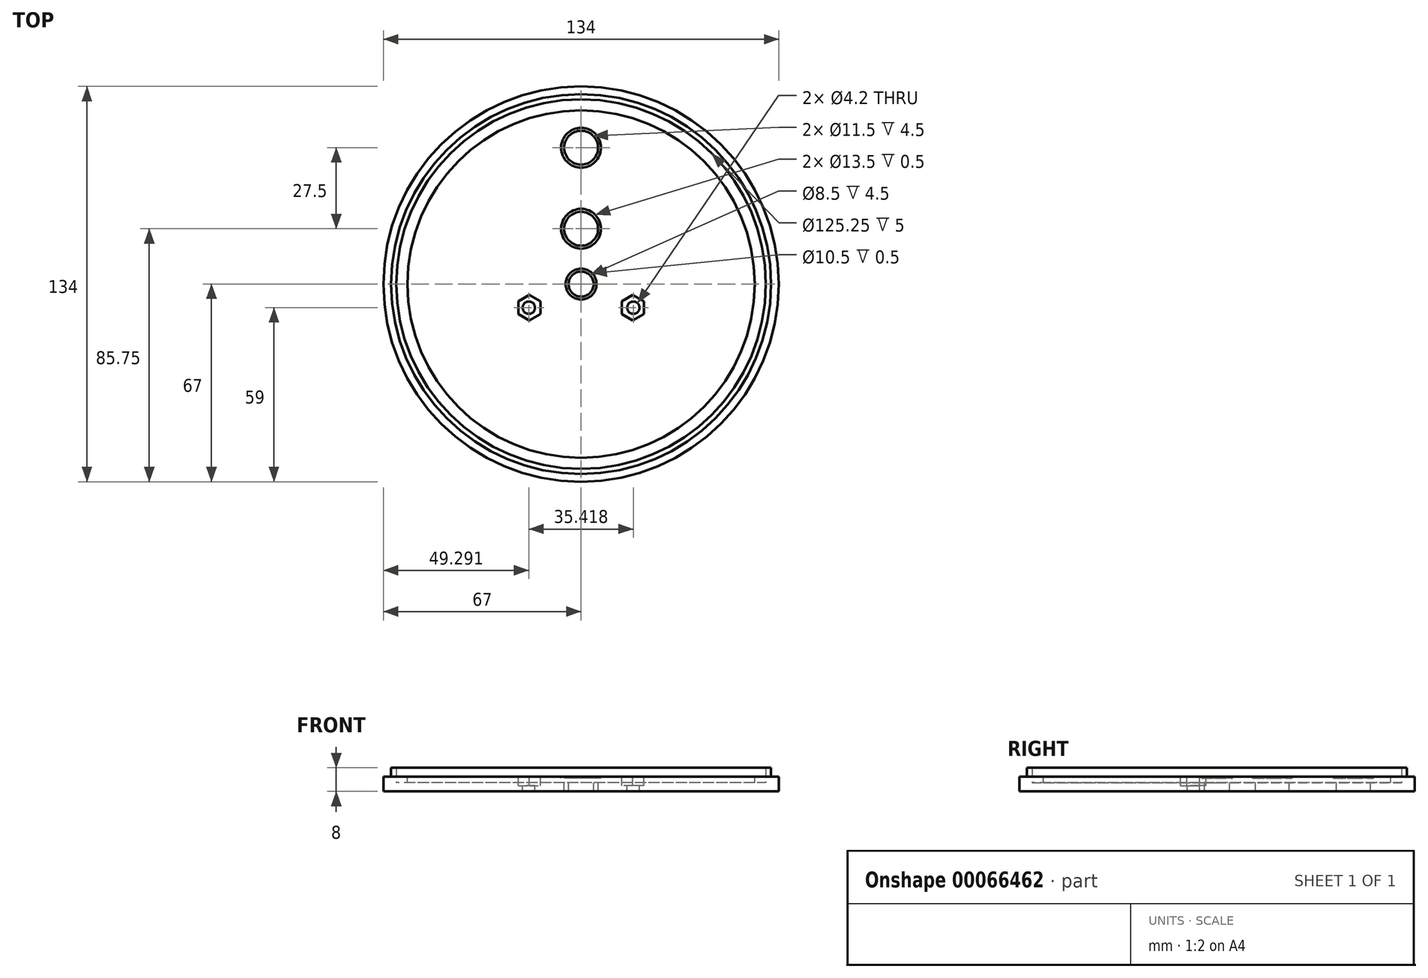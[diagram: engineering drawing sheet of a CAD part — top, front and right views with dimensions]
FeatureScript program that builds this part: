
annotation { "Feature Type Name" : "Feature", "Feature Type Description" : "" }
export const myFeature = defineFeature(function(context is Context, id is Id, definition is map)
    precondition{}
    {
        {
            var Q0;
            Q0=qCreatedBy(makeId("Top.planeOp"),FACE);
            var sketch = newSketch(context, id + "F0", { "sketchPlane" : qUnion([Q0])});
            skCircle(sketch, "E0", {"center": v(0, 0) * mm, "radius": 67 * mm});
            skSolve(sketch);
        }
        {
            var Q0;
            Q0=makeQuery(id+"F0.imprint","IMPRINT",FACE,{"disambiguationData":[TD([[makeQuery(id+"F0.imprint","IMPRINT",EDGE,{"derivedFrom":sQuery(id+"F0.wireOp",EDGE,"E0")}),1.0]])]});
            extrude(context, id + "F1", {"entities" : qUnion([Q0]), "endBound" : BoundingType.SYMMETRIC, "depth" : 5 * mm});
        }
        {
            var Q0;
            Q0=makeQuery(id+"F1.opExtrude","CAP_FACE",FACE,{"disambiguationData":[OSD([sQuery(id+"F0.wireOp",EDGE,"E0")])],"isStart":false});
            var sketch = newSketch(context, id + "F2", { "sketchPlane" : qUnion([Q0])});
            skCircle(sketch, "E1", {"center": v(0, 0) * mm, "radius": 64.38 * mm});
            skSolve(sketch);
        }
        {
            var Q0;
            Q0=makeQuery(id+"F2.imprint","IMPRINT",FACE,{"disambiguationData":[TD([[makeQuery(id+"F2.imprint","IMPRINT",EDGE,{"derivedFrom":sQuery(id+"F2.wireOp",EDGE,"E1")}),1.0]])]});
            var sketch = newSketch(context, id + "F3", { "sketchPlane" : qUnion([Q0])});
            skCircle(sketch, "E2", {"center": v(0, 0) * mm, "radius": 62.62 * mm});
            skSolve(sketch);
        }
        {
            var Q0;
            Q0=makeQuery(id+"F3.imprint","IMPRINT",FACE,{"disambiguationData":[TD([[makeQuery(id+"F3.imprint","IMPRINT",EDGE,{"derivedFrom":sQuery(id+"F3.wireOp",EDGE,"E2")}),-1.0]])]});
            extrude(context, id + "F4", {"entities" : qUnion([Q0]), "operationType" : NewBodyOperationType.ADD, "depth" : 3 * mm});
        }
        {
            var Q0;
            Q0=makeQuery(id+"F3.imprint","IMPRINT",FACE,{"disambiguationData":[TD([[makeQuery(id+"F3.imprint","IMPRINT",EDGE,{"derivedFrom":sQuery(id+"F3.wireOp",EDGE,"E2")}),1.0]])]});
            var sketch = newSketch(context, id + "F5", { "sketchPlane" : qUnion([Q0])});
            skCircle(sketch, "E3", {"center": v(0, 0) * mm, "radius": 58.88 * mm});
            skSolve(sketch);
        }
        {
            var Q0;
            Q0=makeQuery(id+"F5.imprint","IMPRINT",FACE,{"disambiguationData":[TD([[makeQuery(id+"F5.imprint","IMPRINT",EDGE,{"derivedFrom":sQuery(id+"F5.wireOp",EDGE,"E3")}),-1.0]])]});
            extrude(context, id + "F6", {"entities" : qUnion([Q0]), "operationType" : NewBodyOperationType.REMOVE, "oppositeDirection" : true, "depth" : 2 * mm});
        }
        {
            var Q0;
            Q0=makeQuery(id+"F2.imprint","IMPRINT",FACE,{"disambiguationData":[TD([[makeQuery(id+"F2.imprint","IMPRINT",EDGE,{"derivedFrom":sQuery(id+"F2.wireOp",EDGE,"E1")}),-1.0]])]});
            var sketch = newSketch(context, id + "F7", { "sketchPlane" : qUnion([Q0])});
            skCircle(sketch, "E4", {"center": v(0, 0) * mm, "radius": 4.25 * mm});
            skSolve(sketch);
        }
        {
            var Q0;
            Q0 = qSketchRegion(id + "F7", true);
            extrude(context, id + "F8", {"entities" : qUnion([Q0]), "operationType" : NewBodyOperationType.REMOVE, "endBound" : BoundingType.THROUGH_ALL, "oppositeDirection" : true, "depth" : 5 * mm});
        }
        {
            var Q0;
            Q0=makeQuery(id+"F5.imprint","IMPRINT",FACE,{"disambiguationData":[TD([[makeQuery(id+"F5.imprint","IMPRINT",EDGE,{"derivedFrom":sQuery(id+"F5.wireOp",EDGE,"E3")}),1.0]])]});
            var sketch = newSketch(context, id + "F9", { "sketchPlane" : qUnion([Q0])});
            skCircle(sketch, "E5", {"center": v(0, 18.75) * mm, "radius": 5.75 * mm});
            skSolve(sketch);
        }
        {
            var Q0;
            Q0 = qSketchRegion(id + "F9", true);
            extrude(context, id + "F10", {"entities" : qUnion([Q0]), "operationType" : NewBodyOperationType.REMOVE, "endBound" : BoundingType.THROUGH_ALL, "oppositeDirection" : true, "depth" : 25 * mm});
        }
        {
            var Q0;
            Q0=makeQuery(id+"F5.imprint","IMPRINT",FACE,{"disambiguationData":[TD([[makeQuery(id+"F5.imprint","IMPRINT",EDGE,{"derivedFrom":sQuery(id+"F5.wireOp",EDGE,"E3")}),1.0]])]});
            var sketch = newSketch(context, id + "F11", { "sketchPlane" : qUnion([Q0])});
            skCircle(sketch, "E6", {"center": v(0, 46.25) * mm, "radius": 5.75 * mm});
            skCircle(sketch, "E7.0", {"center": v(0, 46.25) * mm, "radius": 6.75 * mm});
            skSolve(sketch);
        }
        {
            var Q0;
            Q0=makeQuery(id+"F11.imprint","IMPRINT",FACE,{"disambiguationData":[TD([[makeQuery(id+"F11.imprint","IMPRINT",EDGE,{"derivedFrom":sQuery(id+"F11.wireOp",EDGE,"E6")}),1.0]])]});
            extrude(context, id + "F12", {"entities" : qUnion([Q0]), "operationType" : NewBodyOperationType.REMOVE, "endBound" : BoundingType.THROUGH_ALL, "oppositeDirection" : true, "depth" : 25 * mm});
        }
        {
            var Q0;
            Q0=makeQuery(id+"F2.imprint","IMPRINT",FACE,{"disambiguationData":[TD([[makeQuery(id+"F2.imprint","IMPRINT",EDGE,{"derivedFrom":sQuery(id+"F2.wireOp",EDGE,"E1")}),1.0]])]});
            var sketch = newSketch(context, id + "F13", { "sketchPlane" : qUnion([Q0])});
            skLineSegment(sketch, "E8", {"start": v(0, 0) * mm, "end": v(-17.5, 0) * mm, "construction": true});
            skSolve(sketch);
        }
        {
            var Q0;
            Q0=makeQuery(id+"F5.imprint","IMPRINT",FACE,{"disambiguationData":[TD([[makeQuery(id+"F5.imprint","IMPRINT",EDGE,{"derivedFrom":sQuery(id+"F5.wireOp",EDGE,"E3")}),1.0]])]});
            var sketch = newSketch(context, id + "F14", { "sketchPlane" : qUnion([Q0])});
            skCircle(sketch, "E9", {"center": v(-17.7, -8) * mm, "radius": 2.1 * mm});
            skLineSegment(sketch, "E10", {"start": v(0, 0) * mm, "end": v(0, -9.4) * mm, "construction": true});
            skCircle(sketch, "E11.MirrorC", {"center": v(17.7, -8) * mm, "radius": 2.1 * mm});
            skSolve(sketch);
        }
        {
            var Q0;
            Q0 = qSketchRegion(id + "F14", true);
            extrude(context, id + "F15", {"entities" : qUnion([Q0]), "operationType" : NewBodyOperationType.REMOVE, "endBound" : BoundingType.THROUGH_ALL, "oppositeDirection" : true, "depth" : 25 * mm});
        }
        {
            var Q0;
            Q0=makeQuery(id+"F5.imprint","IMPRINT",FACE,{"disambiguationData":[TD([[makeQuery(id+"F5.imprint","IMPRINT",EDGE,{"derivedFrom":sQuery(id+"F5.wireOp",EDGE,"E3")}),1.0]])]});
            var sketch = newSketch(context, id + "F16", { "sketchPlane" : qUnion([Q0])});
            skCircle(sketch, "E12.0", {"center": v(0, 0) * mm, "radius": 5.25 * mm});
            skSolve(sketch);
        }
        {
            var Q0;
            Q0=makeQuery(id+"F5.imprint","IMPRINT",FACE,{"disambiguationData":[TD([[makeQuery(id+"F5.imprint","IMPRINT",EDGE,{"derivedFrom":sQuery(id+"F5.wireOp",EDGE,"E3")}),1.0]])]});
            var sketch = newSketch(context, id + "F17", { "sketchPlane" : qUnion([Q0])});
            skCircle(sketch, "E13.cCircle", {"center": v(-17.5, -8) * mm, "radius": 3.75 * mm, "construction": true});
            skLineSegment(sketch, "E13.0", {"start": v(-13.75, -5.83) * mm, "end": v(-13.75, -10.17) * mm});
            skLineSegment(sketch, "E13.1", {"start": v(-13.75, -10.17) * mm, "end": v(-17.5, -12.33) * mm});
            skLineSegment(sketch, "E13.2", {"start": v(-17.5, -12.33) * mm, "end": v(-21.25, -10.17) * mm});
            skLineSegment(sketch, "E13.3", {"start": v(-21.25, -10.17) * mm, "end": v(-21.25, -5.83) * mm});
            skLineSegment(sketch, "E13.4", {"start": v(-21.25, -5.83) * mm, "end": v(-17.5, -3.67) * mm});
            skLineSegment(sketch, "E13.5", {"start": v(-17.5, -3.67) * mm, "end": v(-13.75, -5.83) * mm});
            skPoint(sketch, "E13.0.midPoint", {"position": v(-13.75, -8) * mm});
            skLineSegment(sketch, "E14", {"start": v(-17.5, -8) * mm, "end": v(0, -8) * mm, "construction": true});
            skCircle(sketch, "E15.MirrorC", {"center": v(17.5, -8) * mm, "radius": 3.75 * mm, "construction": true});
            skLineSegment(sketch, "E16.MirrorCS", {"start": v(21.25, -5.83) * mm, "end": v(17.5, -3.67) * mm});
            skLineSegment(sketch, "E17.MirrorCS", {"start": v(17.5, -3.67) * mm, "end": v(13.75, -5.83) * mm});
            skLineSegment(sketch, "E18.MirrorCS", {"start": v(21.25, -10.17) * mm, "end": v(21.25, -5.83) * mm});
            skLineSegment(sketch, "E19.MirrorCS", {"start": v(17.5, -12.33) * mm, "end": v(21.25, -10.17) * mm});
            skLineSegment(sketch, "E20.MirrorCS", {"start": v(13.75, -10.17) * mm, "end": v(17.5, -12.33) * mm});
            skLineSegment(sketch, "E21.MirrorCS", {"start": v(13.75, -5.83) * mm, "end": v(13.75, -10.17) * mm});
            skSolve(sketch);
        }
        {
            var Q0;
            Q0=makeQuery(id+"F16.imprint","IMPRINT",FACE,{"disambiguationData":[TD([[makeQuery(id+"F16.imprint","IMPRINT",EDGE,{"derivedFrom":sQuery(id+"F16.wireOp",EDGE,"E12.0")}),1.0]])]});
            extrude(context, id + "F18", {"entities" : qUnion([Q0]), "operationType" : NewBodyOperationType.REMOVE, "oppositeDirection" : true, "depth" : 0.5 * mm});
        }
        {
            var Q0;
            Q0=makeQuery(id+"F11.imprint","IMPRINT",FACE,{"disambiguationData":[TD([[makeQuery(id+"F11.imprint","IMPRINT",EDGE,{"derivedFrom":sQuery(id+"F11.wireOp",EDGE,"E6")}),-1.0]])]});
            var sketch = newSketch(context, id + "F19", { "sketchPlane" : qUnion([Q0])});
            skCircle(sketch, "E22.0", {"center": v(0, 18.75) * mm, "radius": 6.75 * mm});
            skCircle(sketch, "E23.0", {"center": v(0, 0) * mm, "radius": 67.62 * mm});
            skSolve(sketch);
        }
        {
            var Q0;
            Q0=makeQuery(id+"F19.imprint","IMPRINT",FACE,{"disambiguationData":[TD([[makeQuery(id+"F19.imprint","IMPRINT",EDGE,{"derivedFrom":sQuery(id+"F19.wireOp",EDGE,"E22.0")}),1.0]])]});
            extrude(context, id + "F20", {"entities" : qUnion([Q0]), "operationType" : NewBodyOperationType.REMOVE, "oppositeDirection" : true, "depth" : 0.5 * mm});
        }
        {
            var Q0;
            Q0 = qSketchRegion(id + "F11", true);
            extrude(context, id + "F21", {"entities" : qUnion([Q0]), "operationType" : NewBodyOperationType.REMOVE, "oppositeDirection" : true, "depth" : 0.5 * mm});
        }
        {
            var Q0;
            Q0 = qSketchRegion(id + "F17", true);
            extrude(context, id + "F22", {"entities" : qUnion([Q0]), "operationType" : NewBodyOperationType.REMOVE, "oppositeDirection" : true, "depth" : 3 * mm});
        }
    });
